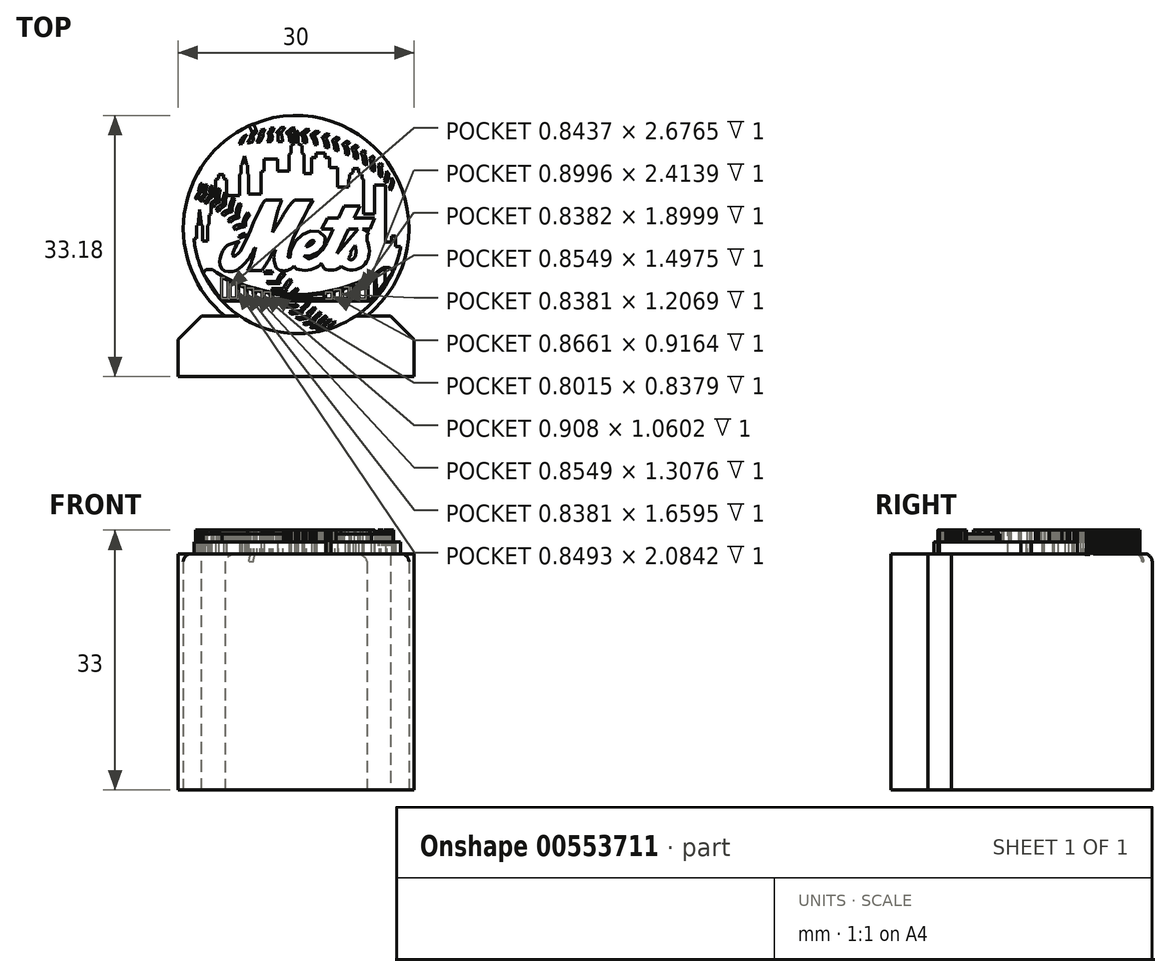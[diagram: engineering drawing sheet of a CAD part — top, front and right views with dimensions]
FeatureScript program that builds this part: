
annotation { "Feature Type Name" : "Feature", "Feature Type Description" : "" }
export const myFeature = defineFeature(function(context is Context, id is Id, definition is map)
    precondition{}
    {
        {
            var Q0;
            Q0=qCreatedBy(makeId("Top.planeOp"),FACE);
            var sketch = newSketch(context, id + "F0", { "sketchPlane" : qUnion([Q0])});
            skLineSegment(sketch, "E0", {"start": v(15.14, 30) * mm, "end": v(15.14, 0) * mm, "construction": true});
            skLineSegment(sketch, "E1", {"start": v(0, 15) * mm, "end": v(30.28, 15) * mm, "construction": true});
            skCircle(sketch, "E2", {"center": v(15.14, 15) * mm, "radius": 14.33 * mm});
            skLineSegment(sketch, "E3.bottom", {"start": v(30.14, -3.85) * mm, "end": v(0.14, -3.85) * mm});
            skLineSegment(sketch, "E3.top", {"start": v(30.14, 3.85) * mm, "end": v(0.14, 3.85) * mm});
            skLineSegment(sketch, "E3.left", {"start": v(30.14, -3.85) * mm, "end": v(30.14, 3.85) * mm});
            skLineSegment(sketch, "E3.right", {"start": v(0.14, -3.85) * mm, "end": v(0.14, 3.85) * mm});
            skPoint(sketch, "E3.middle", {"position": v(15.14, 0) * mm});
            skSolve(sketch);
        }
        {
            var Q0;
            Q0=makeQuery(id+"F0.imprint","IMPRINT",FACE,{"disambiguationData":[TD([[makeQuery(id+"F0.imprint","IMPRINT",EDGE,{"derivedFrom":sQuery(id+"F0.wireOp",EDGE,"E2")}),1.0]])]});
            var sketch = newSketch(context, id + "F1", { "sketchPlane" : qUnion([Q0])});
            skLineSegment(sketch, "E4", {"start": v(2.17, 13.7) * mm, "end": v(2.5, 13.7) * mm});
            skLineSegment(sketch, "E5", {"start": v(2.5, 13.7) * mm, "end": v(2.5, 15.34) * mm});
            skLineSegment(sketch, "E6", {"start": v(2.5, 15.34) * mm, "end": v(2.67, 15.34) * mm});
            skLineSegment(sketch, "E7", {"start": v(2.67, 15.34) * mm, "end": v(2.9, 17.39) * mm});
            skLineSegment(sketch, "E8", {"start": v(2.9, 17.39) * mm, "end": v(3.14, 15.34) * mm});
            skLineSegment(sketch, "E9", {"start": v(3.14, 15.34) * mm, "end": v(3.26, 15.34) * mm});
            skLineSegment(sketch, "E10", {"start": v(3.26, 15.34) * mm, "end": v(3.26, 13.38) * mm});
            skLineSegment(sketch, "E11", {"start": v(3.88, 13.38) * mm, "end": v(3.88, 15.34) * mm});
            skLineSegment(sketch, "E12", {"start": v(3.88, 15.34) * mm, "end": v(4.08, 15.57) * mm});
            skLineSegment(sketch, "E13", {"start": v(4.08, 15.57) * mm, "end": v(4.08, 16.67) * mm});
            skLineSegment(sketch, "E14", {"start": v(4.08, 16.67) * mm, "end": v(4.32, 16.83) * mm});
            skLineSegment(sketch, "E15", {"start": v(4.32, 16.83) * mm, "end": v(4.32, 18.27) * mm});
            skLineSegment(sketch, "E16", {"start": v(4.32, 18.27) * mm, "end": v(4.9, 18.66) * mm});
            skLineSegment(sketch, "E17", {"start": v(4.9, 18.66) * mm, "end": v(4.9, 21.2) * mm});
            skLineSegment(sketch, "E18", {"start": v(4.9, 21.2) * mm, "end": v(5.27, 21.3) * mm});
            skLineSegment(sketch, "E19", {"start": v(5.27, 21.3) * mm, "end": v(5.27, 21.8) * mm});
            skLineSegment(sketch, "E20", {"start": v(5.27, 21.8) * mm, "end": v(5.9, 21.8) * mm});
            skLineSegment(sketch, "E21", {"start": v(5.9, 21.8) * mm, "end": v(5.9, 21.3) * mm});
            skLineSegment(sketch, "E22", {"start": v(5.9, 21.3) * mm, "end": v(6.3, 21.2) * mm});
            skLineSegment(sketch, "E23", {"start": v(6.3, 21.2) * mm, "end": v(6.3, 19.15) * mm});
            skLineSegment(sketch, "E24", {"start": v(6.3, 19.15) * mm, "end": v(7.97, 19.15) * mm});
            skLineSegment(sketch, "E25", {"start": v(7.97, 19.15) * mm, "end": v(7.97, 21.8) * mm});
            skLineSegment(sketch, "E26", {"start": v(7.97, 21.8) * mm, "end": v(8.16, 21.93) * mm});
            skLineSegment(sketch, "E27", {"start": v(8.16, 21.93) * mm, "end": v(8.16, 23.04) * mm});
            skLineSegment(sketch, "E28", {"start": v(8.16, 23.04) * mm, "end": v(8.29, 23.13) * mm});
            skLineSegment(sketch, "E29", {"start": v(8.29, 23.13) * mm, "end": v(8.57, 24.2) * mm});
            skLineSegment(sketch, "E30", {"start": v(8.57, 24.2) * mm, "end": v(8.83, 23.13) * mm});
            skLineSegment(sketch, "E31", {"start": v(8.83, 23.13) * mm, "end": v(8.98, 23.04) * mm});
            skLineSegment(sketch, "E32", {"start": v(8.98, 23.04) * mm, "end": v(8.98, 21.93) * mm});
            skLineSegment(sketch, "E33", {"start": v(8.98, 21.93) * mm, "end": v(9.07, 21.8) * mm});
            skLineSegment(sketch, "E34", {"start": v(9.07, 21.8) * mm, "end": v(9.07, 19.34) * mm});
            skLineSegment(sketch, "E35", {"start": v(9.07, 19.34) * mm, "end": v(10.7, 19.34) * mm});
            skLineSegment(sketch, "E36", {"start": v(10.7, 19.34) * mm, "end": v(10.7, 22.18) * mm});
            skLineSegment(sketch, "E37", {"start": v(10.7, 22.18) * mm, "end": v(11.07, 22.27) * mm});
            skLineSegment(sketch, "E38", {"start": v(11.07, 22.27) * mm, "end": v(11.07, 23.8) * mm});
            skLineSegment(sketch, "E39", {"start": v(11.07, 23.8) * mm, "end": v(12.81, 23.8) * mm});
            skLineSegment(sketch, "E40", {"start": v(12.81, 23.8) * mm, "end": v(12.81, 22.27) * mm});
            skLineSegment(sketch, "E41", {"start": v(12.81, 22.27) * mm, "end": v(14.21, 22.27) * mm});
            skLineSegment(sketch, "E42", {"start": v(14.21, 22.27) * mm, "end": v(14.21, 24.34) * mm});
            skLineSegment(sketch, "E43", {"start": v(14.21, 24.34) * mm, "end": v(14.5, 24.54) * mm});
            skLineSegment(sketch, "E44", {"start": v(14.5, 24.54) * mm, "end": v(14.5, 25.5) * mm});
            skLineSegment(sketch, "E45", {"start": v(14.5, 25.5) * mm, "end": v(14.96, 25.8) * mm});
            skLineSegment(sketch, "E46", {"start": v(14.96, 25.8) * mm, "end": v(14.96, 27.25) * mm});
            skLineSegment(sketch, "E47", {"start": v(14.96, 27.25) * mm, "end": v(15.2, 27.4) * mm});
            skLineSegment(sketch, "E48", {"start": v(15.2, 27.4) * mm, "end": v(15.4, 27.25) * mm});
            skLineSegment(sketch, "E49", {"start": v(15.4, 27.25) * mm, "end": v(15.4, 25.8) * mm});
            skLineSegment(sketch, "E50", {"start": v(15.4, 25.8) * mm, "end": v(15.86, 25.5) * mm});
            skLineSegment(sketch, "E51", {"start": v(15.86, 25.5) * mm, "end": v(15.86, 24.54) * mm});
            skLineSegment(sketch, "E52", {"start": v(15.86, 24.54) * mm, "end": v(16.16, 24.34) * mm});
            skLineSegment(sketch, "E53", {"start": v(16.16, 24.34) * mm, "end": v(16.16, 21.93) * mm});
            skLineSegment(sketch, "E54", {"start": v(16.16, 21.93) * mm, "end": v(17.13, 21.93) * mm});
            skLineSegment(sketch, "E55", {"start": v(17.13, 21.93) * mm, "end": v(17.13, 23.96) * mm});
            skLineSegment(sketch, "E56", {"start": v(17.13, 23.96) * mm, "end": v(17.65, 23.96) * mm});
            skLineSegment(sketch, "E57", {"start": v(17.65, 23.96) * mm, "end": v(17.65, 24.54) * mm});
            skLineSegment(sketch, "E58", {"start": v(17.65, 24.54) * mm, "end": v(18.82, 24.54) * mm});
            skLineSegment(sketch, "E59", {"start": v(18.82, 24.54) * mm, "end": v(18.82, 23.96) * mm});
            skLineSegment(sketch, "E60", {"start": v(18.82, 23.96) * mm, "end": v(19.42, 23.96) * mm});
            skLineSegment(sketch, "E61", {"start": v(19.42, 23.96) * mm, "end": v(19.42, 22.73) * mm});
            skLineSegment(sketch, "E62", {"start": v(19.42, 22.73) * mm, "end": v(20.38, 22.73) * mm});
            skLineSegment(sketch, "E63", {"start": v(20.38, 22.73) * mm, "end": v(20.38, 20.24) * mm});
            skLineSegment(sketch, "E64", {"start": v(20.38, 20.24) * mm, "end": v(21.82, 20.24) * mm});
            skLineSegment(sketch, "E65", {"start": v(21.82, 20.24) * mm, "end": v(21.82, 21.2) * mm});
            skLineSegment(sketch, "E66", {"start": v(21.82, 21.2) * mm, "end": v(21.96, 21.3) * mm});
            skLineSegment(sketch, "E67", {"start": v(21.96, 21.3) * mm, "end": v(21.96, 21.8) * mm});
            skLineSegment(sketch, "E68", {"start": v(21.96, 21.8) * mm, "end": v(22.38, 22.08) * mm});
            skLineSegment(sketch, "E69", {"start": v(22.38, 22.08) * mm, "end": v(22.38, 22.58) * mm});
            skLineSegment(sketch, "E70", {"start": v(22.38, 22.58) * mm, "end": v(23.09, 22.58) * mm});
            skLineSegment(sketch, "E71", {"start": v(23.09, 22.58) * mm, "end": v(23.09, 22.08) * mm});
            skLineSegment(sketch, "E72", {"start": v(23.09, 22.08) * mm, "end": v(23.5, 21.8) * mm});
            skLineSegment(sketch, "E73", {"start": v(23.5, 21.8) * mm, "end": v(23.5, 21.3) * mm});
            skLineSegment(sketch, "E74", {"start": v(23.5, 21.3) * mm, "end": v(23.69, 21.2) * mm});
            skLineSegment(sketch, "E75", {"start": v(23.69, 21.2) * mm, "end": v(23.69, 16.83) * mm});
            skLineSegment(sketch, "E76", {"start": v(23.69, 16.83) * mm, "end": v(25.08, 16.83) * mm});
            skLineSegment(sketch, "E77", {"start": v(25.08, 16.83) * mm, "end": v(25.08, 20.5) * mm});
            skLineSegment(sketch, "E78", {"start": v(25.08, 20.5) * mm, "end": v(26.53, 20.5) * mm});
            skLineSegment(sketch, "E79", {"start": v(26.53, 20.5) * mm, "end": v(26.53, 13.29) * mm});
            skLineSegment(sketch, "E80", {"start": v(26.53, 13.29) * mm, "end": v(27.26, 13.29) * mm});
            skLineSegment(sketch, "E81", {"start": v(27.26, 13.29) * mm, "end": v(27.26, 14) * mm});
            skLineSegment(sketch, "E82", {"start": v(27.26, 14) * mm, "end": v(27.74, 14) * mm});
            skLineSegment(sketch, "E83", {"start": v(27.74, 14) * mm, "end": v(27.74, 12.66) * mm});
            skLineSegment(sketch, "E84", {"start": v(27.74, 12.66) * mm, "end": v(28.41, 12.66) * mm});
            skArc(sketch, "E85", {"start": v(2.17, 13.7) * mm, "mid": v(14.83, 1.63) * mm, "end": v(28.41, 12.66) * mm});
            skLineSegment(sketch, "E86", {"start": v(3.26, 13.38) * mm, "end": v(3.88, 13.38) * mm});
            skSolve(sketch);
        }
        {
            var Q0;
            Q0=makeQuery(id+"F0.imprint","IMPRINT",FACE,{"disambiguationData":[TD([[makeQuery(id+"F0.imprint","IMPRINT",EDGE,{"derivedFrom":sQuery(id+"F0.wireOp",EDGE,"E2")}),1.0]])]});
            var sketch = newSketch(context, id + "F2", { "sketchPlane" : qUnion([Q0])});
            skLineSegment(sketch, "E87", {"start": v(11.25, 18.59) * mm, "end": v(13.33, 18.59) * mm});
            skFitSpline(sketch, "E88", {"points": [v(13.33, 18.59) * mm, v(13.16, 18.19) * mm, v(12.79, 17.17) * mm, v(12.52, 16.09) * mm], "startDerivative": vector(-0.65, -1.46) * mm, "endDerivative": vector(-0.62, -2.77) * mm});
            skLineSegment(sketch, "E89", {"start": v(12.52, 16.09) * mm, "end": v(12.14, 14.47) * mm});
            skFitSpline(sketch, "E90", {"points": [v(12.14, 14.47) * mm, v(12.55, 15.14) * mm, v(13.14, 16.08) * mm, v(13.74, 17.05) * mm, v(14.35, 17.93) * mm, v(14.92, 18.59) * mm], "startDerivative": vector(2.21, 3.58) * mm, "endDerivative": vector(3.06, 3.36) * mm});
            skLineSegment(sketch, "E91", {"start": v(14.92, 18.59) * mm, "end": v(17.26, 18.59) * mm});
            skFitSpline(sketch, "E92", {"points": [v(17.26, 18.59) * mm, v(16.82, 17.86) * mm, v(16.11, 16.48) * mm, v(15.3, 14.87) * mm, v(14.62, 13.31) * mm, v(14.19, 12.01) * mm, v(14.15, 11.26) * mm, v(14.28, 11.16) * mm, v(14.38, 11.2) * mm, v(14.4, 11.47) * mm, v(14.53, 12.4) * mm, v(15.1, 13.42) * mm, v(15.87, 14.15) * mm, v(16.83, 14.6) * mm, v(17.7, 14.67) * mm, v(18.49, 14.32) * mm, v(18.9, 13.57) * mm, v(18.6, 12.67) * mm, v(17.94, 12) * mm, v(17.26, 11.64) * mm, v(16.34, 11.43) * mm, v(16.16, 11.44) * mm, v(16.35, 11.18) * mm, v(16.97, 11.16) * mm, v(17.86, 11.6) * mm, v(18.4, 12.16) * mm, v(18.9, 12.9) * mm, v(19.3, 13.69) * mm, v(19.72, 14.57) * mm, v(19.85, 14.9) * mm], "startDerivative": vector(-11.95, -18.74) * mm, "endDerivative": vector(4.49, 12.3) * mm});
            skLineSegment(sketch, "E93", {"start": v(19.85, 14.9) * mm, "end": v(18.38, 14.9) * mm});
            skLineSegment(sketch, "E94", {"start": v(18.38, 14.9) * mm, "end": v(19.11, 16.29) * mm});
            skLineSegment(sketch, "E95", {"start": v(19.11, 16.29) * mm, "end": v(20.53, 16.29) * mm});
            skLineSegment(sketch, "E96", {"start": v(20.53, 16.29) * mm, "end": v(21.26, 17.85) * mm});
            skLineSegment(sketch, "E97", {"start": v(21.26, 17.85) * mm, "end": v(23.24, 17.85) * mm});
            skLineSegment(sketch, "E98", {"start": v(23.24, 17.85) * mm, "end": v(22.51, 16.29) * mm});
            skLineSegment(sketch, "E99", {"start": v(22.51, 16.29) * mm, "end": v(25.07, 16.29) * mm});
            skLineSegment(sketch, "E100", {"start": v(25.07, 16.29) * mm, "end": v(24.52, 14.9) * mm});
            skLineSegment(sketch, "E101", {"start": v(24.52, 14.9) * mm, "end": v(23.6, 14.9) * mm});
            skLineSegment(sketch, "E102", {"start": v(23.6, 14.9) * mm, "end": v(24.38, 14.48) * mm});
            skFitSpline(sketch, "E103", {"points": [v(24.38, 14.48) * mm, v(24.14, 14.06) * mm, v(24.2, 13.36) * mm, v(24.42, 12.5) * mm, v(24.38, 11.45) * mm, v(24.01, 10.62) * mm, v(23.3, 9.99) * mm, v(22.4, 9.73) * mm, v(21.45, 9.83) * mm, v(20.86, 10.21) * mm], "startDerivative": vector(-3.57, -4.54) * mm, "endDerivative": vector(-5.2, 4.27) * mm});
            skFitSpline(sketch, "E104", {"points": [v(20.86, 10.21) * mm, v(20.5, 9.88) * mm, v(19.8, 9.72) * mm, v(18.98, 9.78) * mm, v(18.54, 10.11) * mm, v(18.3, 10.5) * mm, v(18.02, 10.21) * mm, v(17.31, 9.87) * mm, v(16.27, 9.66) * mm, v(15.21, 9.86) * mm, v(14.85, 10.21) * mm], "startDerivative": vector(-3.77, -4.27) * mm, "endDerivative": vector(-3.25, 4.4) * mm});
            skFitSpline(sketch, "E105", {"points": [v(14.85, 10.21) * mm, v(14.47, 9.85) * mm, v(13.77, 9.6) * mm, v(12.9, 9.74) * mm, v(12.5, 10.25) * mm, v(12.31, 11) * mm, v(12.34, 11.75) * mm, v(12.5, 12.33) * mm], "startDerivative": vector(-2.74, -3.06) * mm, "endDerivative": vector(1.37, 4.22) * mm});
            skFitSpline(sketch, "E106", {"points": [v(12.5, 12.33) * mm, v(12.2, 11.97) * mm, v(11.81, 11.26) * mm, v(11.34, 10.46) * mm, v(10.79, 9.66) * mm], "startDerivative": vector(-1.57, -1.66) * mm, "endDerivative": vector(-2, -2.88) * mm});
            skLineSegment(sketch, "E107", {"start": v(10.79, 9.66) * mm, "end": v(8.95, 9.66) * mm});
            skFitSpline(sketch, "E108", {"points": [v(8.95, 9.66) * mm, v(9.23, 10.1) * mm, v(9.6, 11.13) * mm, v(9.87, 12.07) * mm, v(9.98, 12.53) * mm], "startDerivative": vector(1.33, 1.86) * mm, "endDerivative": vector(0.48, 2.12) * mm});
            skFitSpline(sketch, "E109", {"points": [v(9.98, 12.53) * mm, v(9.87, 12.49) * mm, v(9.7, 12.08) * mm, v(9.37, 11.52) * mm, v(8.95, 10.9) * mm, v(8.22, 10.12) * mm, v(7.56, 9.66) * mm, v(6.69, 9.48) * mm, v(5.8, 9.75) * mm, v(5.44, 10.5) * mm, v(5.5, 11.17) * mm, v(5.75, 11.94) * mm, v(6.26, 12.74) * mm, v(6.49, 12.9) * mm, v(7.95, 13.4) * mm], "startDerivative": vector(-4.02, -0.49) * mm, "endDerivative": vector(17.33, 5.86) * mm});
            skFitSpline(sketch, "E110", {"points": [v(7.95, 13.4) * mm, v(7.69, 13.04) * mm, v(7.38, 12.53) * mm, v(7.14, 11.96) * mm, v(7.1, 11.57) * mm, v(7.24, 11.43) * mm, v(7.63, 11.65) * mm, v(8.12, 12.28) * mm, v(8.95, 13.9) * mm, v(9.58, 15.35) * mm, v(10.18, 16.7) * mm, v(10.99, 18.3) * mm, v(11.25, 18.59) * mm], "startDerivative": vector(-4.1, -5.58) * mm, "endDerivative": vector(4.03, 3.58) * mm});
            skSolve(sketch);
        }
        {
            var Q0;
            Q0=qSketchRegion(id+"F0",true);
            extrude(context, id + "F3", {"entities" : qUnion([Q0]), "depth" : 30 * mm, "offsetDistance" : 25.4 * mm});
        }
        {
            var Q0;
            Q0=qSketchRegion(id+"F1",true);
            extrude(context, id + "F4", {"entities" : qUnion([Q0]), "operationType" : NewBodyOperationType.ADD, "depth" : 31.5 * mm, "offsetDistance" : 25.4 * mm});
        }
        {
            var Q0;
            Q0=makeQuery(id+"F3.opExtrude","CAP_FACE",FACE,{"disambiguationData":[OSD([sQuery(id+"F0.wireOp",EDGE,"E2")])],"isStart":false});
            var sketch = newSketch(context, id + "F5", { "sketchPlane" : qUnion([Q0])});
            skFitSpline(sketch, "E111", {"points": [v(16.4, 12.67) * mm, v(16.47, 12.86) * mm, v(16.72, 13.14) * mm, v(17.02, 13.37) * mm, v(17.35, 13.43) * mm, v(17.42, 13.34) * mm, v(17.31, 13.15) * mm, v(16.98, 12.9) * mm, v(16.64, 12.72) * mm, v(16.4, 12.67) * mm]});
            skLineSegment(sketch, "E112", {"start": v(20.32, 11.78) * mm, "end": v(21.8, 14.92) * mm});
            skLineSegment(sketch, "E113", {"start": v(21.8, 14.92) * mm, "end": v(22.98, 14.92) * mm});
            skLineSegment(sketch, "E114", {"start": v(22.98, 14.92) * mm, "end": v(20.32, 11.78) * mm});
            skLineSegment(sketch, "E115", {"start": v(22, 11.95) * mm, "end": v(22.63, 12.83) * mm});
            skFitSpline(sketch, "E116", {"points": [v(22.63, 12.83) * mm, v(22.68, 12.73) * mm, v(22.71, 12.47) * mm, v(22.73, 12) * mm, v(22.68, 11.54) * mm, v(22.52, 11.25) * mm, v(22.2, 11.01) * mm, v(21.9, 11.05) * mm, v(21.83, 11.25) * mm, v(21.97, 11.51) * mm, v(22.19, 11.74) * mm], "startDerivative": vector(0.88, -1.53) * mm, "endDerivative": vector(2.11, 2.19) * mm});
            skLineSegment(sketch, "E117", {"start": v(22.19, 11.74) * mm, "end": v(22, 11.95) * mm});
            skSolve(sketch);
        }
        {
            var Q0;
            Q0=qSketchRegion(id+"F2",true);
            extrude(context, id + "F6", {"entities" : qUnion([Q0]), "operationType" : NewBodyOperationType.ADD, "depth" : 33 * mm, "offsetDistance" : 25.4 * mm});
        }
        {
            var Q0;
            Q0=qSketchRegion(id+"F5",true);
            extrude(context, id + "F7", {"entities" : qUnion([Q0]), "operationType" : NewBodyOperationType.REMOVE, "depth" : 25.4 * mm, "offsetDistance" : 25.4 * mm});
        }
        {
            var Q0;
            Q0=makeQuery(id+"F3.opExtrude","CAP_FACE",FACE,{"disambiguationData":[OSD([sQuery(id+"F0.wireOp",EDGE,"E2")])],"isStart":false});
            var sketch = newSketch(context, id + "F8", { "sketchPlane" : qUnion([Q0])});
            skLineSegment(sketch, "E118", {"start": v(3.02, 20.66) * mm, "end": v(3.17, 20.66) * mm});
            skFitSpline(sketch, "E119", {"points": [v(3.17, 20.66) * mm, v(3.1, 20.34) * mm, v(2.99, 19.94) * mm, v(3.08, 19.57) * mm], "startDerivative": vector(-0.2, -0.98) * mm, "endDerivative": vector(0.43, -1.08) * mm});
            skFitSpline(sketch, "E120", {"points": [v(3.08, 19.57) * mm, v(2.89, 19.37) * mm, v(2.67, 18.96) * mm, v(2.55, 18.65) * mm], "startDerivative": vector(-0.64, -0.58) * mm, "endDerivative": vector(-0.32, -0.88) * mm});
            skLineSegment(sketch, "E121", {"start": v(2.55, 18.65) * mm, "end": v(2.36, 18.77) * mm});
            skFitSpline(sketch, "E122", {"points": [v(2.36, 18.77) * mm, v(2.48, 19.12) * mm, v(2.66, 19.41) * mm, v(2.84, 19.61) * mm], "startDerivative": vector(0.3, 1) * mm, "endDerivative": vector(0.6, 0.6) * mm});
            skFitSpline(sketch, "E123", {"points": [v(2.84, 19.61) * mm, v(2.78, 19.78) * mm, v(2.84, 20.15) * mm, v(2.9, 20.34) * mm, v(3.02, 20.66) * mm], "startDerivative": vector(-0.4, 0.7) * mm, "endDerivative": vector(0.4, 1.24) * mm});
            skLineSegment(sketch, "E124", {"start": v(3.55, 20.59) * mm, "end": v(3.84, 20.51) * mm});
            skFitSpline(sketch, "E125", {"points": [v(3.84, 20.51) * mm, v(3.71, 19.96) * mm, v(3.66, 19.55) * mm, v(3.74, 19.3) * mm], "startDerivative": vector(-0.33, -1.42) * mm, "endDerivative": vector(0.4, -0.87) * mm});
            skFitSpline(sketch, "E126", {"points": [v(3.74, 19.3) * mm, v(3.54, 19.08) * mm, v(3.3, 18.76) * mm, v(3.13, 18.4) * mm], "startDerivative": vector(-0.6, -0.74) * mm, "endDerivative": vector(-0.38, -1.09) * mm});
            skLineSegment(sketch, "E127", {"start": v(3.13, 18.4) * mm, "end": v(2.93, 18.52) * mm});
            skFitSpline(sketch, "E128", {"points": [v(2.93, 18.52) * mm, v(3.07, 18.88) * mm, v(3.47, 19.32) * mm], "startDerivative": vector(0.22, 0.82) * mm, "endDerivative": vector(0.84, 0.79) * mm});
            skFitSpline(sketch, "E129", {"points": [v(3.47, 19.32) * mm, v(3.38, 19.62) * mm, v(3.4, 20.05) * mm, v(3.55, 20.59) * mm], "startDerivative": vector(-0.36, 1) * mm, "endDerivative": vector(0.44, 1.42) * mm});
            skLineSegment(sketch, "E130", {"start": v(4.32, 20.4) * mm, "end": v(4.6, 20.26) * mm});
            skFitSpline(sketch, "E131", {"points": [v(4.6, 20.26) * mm, v(4.5, 19.85) * mm, v(4.45, 19.32) * mm, v(4.52, 18.96) * mm], "startDerivative": vector(-0.32, -1.18) * mm, "endDerivative": vector(0.3, -1.1) * mm});
            skFitSpline(sketch, "E132", {"points": [v(4.52, 18.96) * mm, v(4.32, 18.83) * mm, v(4.05, 18.58) * mm, v(3.8, 18.13) * mm], "startDerivative": vector(-0.7, -0.44) * mm, "endDerivative": vector(-0.54, -1.23) * mm});
            skLineSegment(sketch, "E133", {"start": v(3.8, 18.13) * mm, "end": v(3.5, 18.27) * mm});
            skFitSpline(sketch, "E134", {"points": [v(3.5, 18.27) * mm, v(3.64, 18.53) * mm, v(3.98, 18.91) * mm, v(4.17, 19.05) * mm], "startDerivative": vector(0.38, 0.76) * mm, "endDerivative": vector(0.65, 0.37) * mm});
            skFitSpline(sketch, "E135", {"points": [v(4.17, 19.05) * mm, v(4.12, 19.36) * mm, v(4.17, 19.92) * mm, v(4.32, 20.4) * mm], "startDerivative": vector(-0.24, 1.02) * mm, "endDerivative": vector(0.47, 1.3) * mm});
            skLineSegment(sketch, "E136", {"start": v(5.2, 20.05) * mm, "end": v(5.5, 19.9) * mm});
            skFitSpline(sketch, "E137", {"points": [v(5.5, 19.9) * mm, v(5.42, 19.54) * mm, v(5.38, 18.87) * mm, v(5.53, 18.4) * mm], "startDerivative": vector(-0.3, -1.13) * mm, "endDerivative": vector(0.6, -1.3) * mm});
            skFitSpline(sketch, "E138", {"points": [v(5.53, 18.4) * mm, v(5.29, 18.3) * mm, v(4.97, 18.05) * mm, v(4.64, 17.64) * mm], "startDerivative": vector(-0.87, -0.3) * mm, "endDerivative": vector(-0.82, -1.1) * mm});
            skLineSegment(sketch, "E139", {"start": v(4.64, 17.64) * mm, "end": v(4.37, 17.85) * mm});
            skFitSpline(sketch, "E140", {"points": [v(4.37, 17.85) * mm, v(4.43, 18.04) * mm, v(4.8, 18.37) * mm, v(5.16, 18.57) * mm], "startDerivative": vector(0.13, 0.73) * mm, "endDerivative": vector(0.96, 0.49) * mm});
            skFitSpline(sketch, "E141", {"points": [v(5.16, 18.57) * mm, v(5.1, 18.97) * mm, v(5.06, 19.58) * mm, v(5.2, 20.05) * mm], "startDerivative": vector(-0.23, 1.25) * mm, "endDerivative": vector(0.52, 1.35) * mm});
            skLineSegment(sketch, "E142", {"start": v(6.07, 19.58) * mm, "end": v(6.4, 19.42) * mm});
            skFitSpline(sketch, "E143", {"points": [v(6.4, 19.42) * mm, v(6.32, 19.2) * mm, v(6.23, 18.88) * mm, v(6.16, 18.29) * mm, v(6.22, 17.95) * mm], "startDerivative": vector(-0.36, -1.04) * mm, "endDerivative": vector(0.37, -1.27) * mm});
            skFitSpline(sketch, "E144", {"points": [v(6.22, 17.95) * mm, v(5.96, 17.82) * mm, v(5.6, 17.53) * mm, v(5.52, 17.44) * mm, v(5.34, 17.15) * mm], "startDerivative": vector(-0.95, -0.37) * mm, "endDerivative": vector(-0.78, -1.25) * mm});
            skLineSegment(sketch, "E145", {"start": v(5.34, 17.15) * mm, "end": v(5.05, 17.34) * mm});
            skFitSpline(sketch, "E146", {"points": [v(5.05, 17.34) * mm, v(5.11, 17.57) * mm, v(5.56, 17.94) * mm, v(5.9, 18.13) * mm], "startDerivative": vector(0.05, 0.86) * mm, "endDerivative": vector(0.96, 0.5) * mm});
            skFitSpline(sketch, "E147", {"points": [v(5.9, 18.13) * mm, v(5.84, 18.46) * mm, v(5.9, 18.98) * mm, v(6.07, 19.58) * mm], "startDerivative": vector(-0.32, 1.11) * mm, "endDerivative": vector(0.47, 1.59) * mm});
            skLineSegment(sketch, "E148", {"start": v(7.06, 18.88) * mm, "end": v(7.37, 18.65) * mm});
            skPoint(sketch, "E149.1.internal.snap0", {"position": v(7.22, 18.76) * mm});
            skFitSpline(sketch, "E149", {"points": [v(7.37, 18.65) * mm, v(7.22, 18.36) * mm, v(7.05, 17.8) * mm, v(6.98, 17.34) * mm, v(7.1, 17.18) * mm], "startDerivative": vector(-0.7, -1.12) * mm, "endDerivative": vector(0.8, -0.76) * mm});
            skFitSpline(sketch, "E150", {"points": [v(7.1, 17.18) * mm, v(6.85, 17.1) * mm, v(6.42, 16.94) * mm, v(6, 16.61) * mm], "startDerivative": vector(-0.86, -0.28) * mm, "endDerivative": vector(-1.07, -0.96) * mm});
            skLineSegment(sketch, "E151", {"start": v(6, 16.61) * mm, "end": v(5.7, 16.82) * mm});
            skFitSpline(sketch, "E152", {"points": [v(5.7, 16.82) * mm, v(5.9, 17.06) * mm, v(6.38, 17.29) * mm, v(6.83, 17.45) * mm], "startDerivative": vector(0.55, 0.92) * mm, "endDerivative": vector(1.23, 0.43) * mm});
            skFitSpline(sketch, "E153", {"points": [v(6.83, 17.45) * mm, v(6.72, 17.6) * mm, v(6.74, 18.04) * mm, v(6.88, 18.47) * mm, v(7.06, 18.88) * mm], "startDerivative": vector(-0.74, 0.74) * mm, "endDerivative": vector(0.7, 1.48) * mm});
            skLineSegment(sketch, "E154", {"start": v(7.9, 18.24) * mm, "end": v(8.2, 17.95) * mm});
            skFitSpline(sketch, "E155", {"points": [v(8.2, 17.95) * mm, v(8.07, 17.72) * mm, v(7.88, 17.04) * mm, v(7.82, 16.59) * mm, v(7.92, 16.35) * mm], "startDerivative": vector(-0.64, -0.94) * mm, "endDerivative": vector(0.6, -1.12) * mm});
            skFitSpline(sketch, "E156", {"points": [v(7.92, 16.35) * mm, v(7.63, 16.28) * mm, v(7.2, 16.07) * mm, v(6.87, 15.86) * mm, v(6.75, 15.72) * mm], "startDerivative": vector(-1.15, -0.2) * mm, "endDerivative": vector(-0.55, -0.71) * mm});
            skLineSegment(sketch, "E157", {"start": v(6.75, 15.72) * mm, "end": v(6.51, 16.01) * mm});
            skFitSpline(sketch, "E158", {"points": [v(6.51, 16.01) * mm, v(6.66, 16.2) * mm, v(7.14, 16.48) * mm, v(7.61, 16.66) * mm], "startDerivative": vector(0.45, 0.77) * mm, "endDerivative": vector(1.25, 0.43) * mm});
            skFitSpline(sketch, "E159", {"points": [v(7.61, 16.66) * mm, v(7.55, 16.8) * mm, v(7.57, 17.34) * mm, v(7.72, 17.86) * mm, v(7.9, 18.24) * mm], "startDerivative": vector(-0.47, 0.78) * mm, "endDerivative": vector(0.7, 1.44) * mm});
            skLineSegment(sketch, "E160", {"start": v(8.98, 17) * mm, "end": v(9.24, 16.67) * mm});
            skFitSpline(sketch, "E161", {"points": [v(9.24, 16.67) * mm, v(9.04, 16.4) * mm, v(8.74, 15.84) * mm, v(8.7, 15.36) * mm, v(8.72, 15.24) * mm], "startDerivative": vector(-0.8, -0.96) * mm, "endDerivative": vector(0.17, -0.68) * mm});
            skFitSpline(sketch, "E162", {"points": [v(8.72, 15.24) * mm, v(8.46, 15.19) * mm, v(7.87, 15.04) * mm, v(7.44, 14.8) * mm], "startDerivative": vector(-0.89, -0.18) * mm, "endDerivative": vector(-1.11, -0.76) * mm});
            skLineSegment(sketch, "E163", {"start": v(7.44, 14.8) * mm, "end": v(7.18, 15.12) * mm});
            skFitSpline(sketch, "E164", {"points": [v(7.18, 15.12) * mm, v(7.57, 15.4) * mm, v(8.17, 15.48) * mm, v(8.45, 15.55) * mm], "startDerivative": vector(0.97, 0.97) * mm, "endDerivative": vector(0.89, 0.32) * mm});
            skFitSpline(sketch, "E165", {"points": [v(8.45, 15.55) * mm, v(8.38, 15.75) * mm, v(8.49, 16.1) * mm, v(8.62, 16.45) * mm, v(8.98, 17) * mm], "startDerivative": vector(-0.56, 0.99) * mm, "endDerivative": vector(1.3, 1.73) * mm});
            skLineSegment(sketch, "E166", {"start": v(7.86, 14.02) * mm, "end": v(7.98, 13.74) * mm});
            skFitSpline(sketch, "E167", {"points": [v(7.98, 13.74) * mm, v(8.22, 13.86) * mm, v(8.68, 14.01) * mm], "startDerivative": vector(0.52, 0.3) * mm, "endDerivative": vector(0.88, 0.26) * mm});
            skLineSegment(sketch, "E168", {"start": v(8.68, 14.01) * mm, "end": v(8.68, 14.34) * mm});
            skFitSpline(sketch, "E169", {"points": [v(8.68, 14.34) * mm, v(8.35, 14.27) * mm, v(7.86, 14.02) * mm], "startDerivative": vector(-0.73, -0.1) * mm, "endDerivative": vector(-0.9, -0.54) * mm});
            skLineSegment(sketch, "E170", {"start": v(11.27, 9.54) * mm, "end": v(11.05, 9.26) * mm});
            skLineSegment(sketch, "E171", {"start": v(11.05, 9.26) * mm, "end": v(12.14, 9.26) * mm});
            skLineSegment(sketch, "E172", {"start": v(11.27, 9.54) * mm, "end": v(12.07, 9.54) * mm});
            skLineSegment(sketch, "E173", {"start": v(12.07, 9.54) * mm, "end": v(12.14, 9.26) * mm});
            skLineSegment(sketch, "E174", {"start": v(11.38, 8.25) * mm, "end": v(11.62, 7.93) * mm});
            skLineSegment(sketch, "E175", {"start": v(11.62, 7.93) * mm, "end": v(13.11, 7.96) * mm});
            skFitSpline(sketch, "E176", {"points": [v(13.11, 7.96) * mm, v(13.07, 8.08) * mm, v(13.06, 8.37) * mm, v(13.4, 8.79) * mm, v(13.79, 9.25) * mm], "startDerivative": vector(-0.34, 0.71) * mm, "endDerivative": vector(1.18, 1.44) * mm});
            skLineSegment(sketch, "E177", {"start": v(13.79, 9.25) * mm, "end": v(13.31, 9.28) * mm});
            skFitSpline(sketch, "E178", {"points": [v(13.31, 9.28) * mm, v(13.07, 9.05) * mm, v(12.78, 8.52) * mm, v(12.75, 8.33) * mm], "startDerivative": vector(-0.73, -0.58) * mm, "endDerivative": vector(0, -0.67) * mm});
            skLineSegment(sketch, "E179", {"start": v(11.38, 8.25) * mm, "end": v(12.75, 8.33) * mm});
            skLineSegment(sketch, "E180", {"start": v(14.36, 8.56) * mm, "end": v(14.63, 8.22) * mm});
            skFitSpline(sketch, "E181", {"points": [v(14.63, 8.22) * mm, v(14.35, 7.95) * mm, v(13.93, 7.36) * mm, v(13.83, 7.23) * mm, v(14, 6.98) * mm], "startDerivative": vector(-1.06, -0.8) * mm, "endDerivative": vector(1.15, -1.24) * mm});
            skFitSpline(sketch, "E182", {"points": [v(14, 6.98) * mm, v(13.85, 6.93) * mm, v(13.4, 6.98) * mm, v(12.8, 6.98) * mm, v(12.21, 6.98) * mm], "startDerivative": vector(-0.87, -0.44) * mm, "endDerivative": vector(-1.99, 0.03) * mm});
            skLineSegment(sketch, "E183", {"start": v(12.21, 6.98) * mm, "end": v(12, 7.32) * mm});
            skLineSegment(sketch, "E184", {"start": v(12, 7.32) * mm, "end": v(13.55, 7.32) * mm});
            skFitSpline(sketch, "E185", {"points": [v(13.55, 7.32) * mm, v(13.6, 7.54) * mm, v(13.78, 7.88) * mm, v(14.09, 8.29) * mm, v(14.36, 8.56) * mm], "startDerivative": vector(0.17, 1.08) * mm, "endDerivative": vector(1.05, 1) * mm});
            skLineSegment(sketch, "E186", {"start": v(15.18, 7.45) * mm, "end": v(15.4, 7.24) * mm});
            skFitSpline(sketch, "E187", {"points": [v(15.4, 7.24) * mm, v(15.23, 7) * mm, v(14.8, 6.6) * mm, v(14.5, 6.76) * mm], "startDerivative": vector(-0.49, -0.72) * mm, "endDerivative": vector(-0.92, 0.87) * mm});
            skLineSegment(sketch, "E188", {"start": v(14.5, 6.76) * mm, "end": v(15.18, 7.45) * mm});
            skLineSegment(sketch, "E189", {"start": v(13.55, 5.26) * mm, "end": v(13.77, 5) * mm});
            skLineSegment(sketch, "E190", {"start": v(13.77, 5) * mm, "end": v(14.73, 5) * mm});
            skFitSpline(sketch, "E191", {"points": [v(14.73, 5) * mm, v(15.33, 5.1) * mm, v(15.4, 5.2) * mm], "startDerivative": vector(1.08, 0.09) * mm, "endDerivative": vector(0.11, 0.34) * mm});
            skLineSegment(sketch, "E192", {"start": v(15.4, 5.2) * mm, "end": v(15.21, 5.35) * mm});
            skFitSpline(sketch, "E193", {"points": [v(13.55, 5.26) * mm, v(14.09, 5.26) * mm, v(14.81, 5.26) * mm, v(15.21, 5.35) * mm], "startDerivative": vector(1.52, 0.02) * mm, "endDerivative": vector(1.25, 0.39) * mm});
            skLineSegment(sketch, "E194", {"start": v(15.68, 4.81) * mm, "end": v(15.89, 4.6) * mm});
            skFitSpline(sketch, "E195", {"points": [v(15.89, 4.6) * mm, v(16.18, 4.75) * mm, v(16.73, 5.31) * mm, v(16.88, 5.54) * mm], "startDerivative": vector(0.9, 0.38) * mm, "endDerivative": vector(0.4, 0.75) * mm});
            skLineSegment(sketch, "E196", {"start": v(16.88, 5.54) * mm, "end": v(16.63, 5.76) * mm});
            skFitSpline(sketch, "E197", {"points": [v(15.68, 4.81) * mm, v(16.03, 5.04) * mm, v(16.38, 5.4) * mm, v(16.63, 5.76) * mm], "startDerivative": vector(1.11, 0.64) * mm, "endDerivative": vector(0.71, 1.1) * mm});
            skLineSegment(sketch, "E198", {"start": v(14.25, 4.43) * mm, "end": v(14.51, 4.14) * mm});
            skLineSegment(sketch, "E199", {"start": v(15.06, 3.67) * mm, "end": v(15.44, 3.39) * mm});
            skFitSpline(sketch, "E200", {"points": [v(15.44, 3.39) * mm, v(15.92, 3.45) * mm, v(16.94, 3.69) * mm], "startDerivative": vector(1.08, 0.11) * mm, "endDerivative": vector(1.88, 0.46) * mm});
            skFitSpline(sketch, "E201", {"points": [v(15.06, 3.67) * mm, v(15.73, 3.67) * mm, v(16.66, 3.92) * mm], "startDerivative": vector(1.43, -0.1) * mm, "endDerivative": vector(1.77, 0.59) * mm});
            skLineSegment(sketch, "E202", {"start": v(17.4, 5.01) * mm, "end": v(17.62, 4.81) * mm});
            skPoint(sketch, "E203.2.internal.snap0", {"position": v(16.8, 3.8) * mm});
            skLineSegment(sketch, "E204", {"start": v(16.66, 3.92) * mm, "end": v(16.47, 4.08) * mm});
            skLineSegment(sketch, "E205", {"start": v(16.47, 4.08) * mm, "end": v(17.4, 5.01) * mm});
            skLineSegment(sketch, "E206", {"start": v(16.04, 2.93) * mm, "end": v(16.41, 2.74) * mm});
            skLineSegment(sketch, "E207", {"start": v(18.09, 4.39) * mm, "end": v(18.36, 4.17) * mm});
            skFitSpline(sketch, "E208", {"points": [v(17.22, 3.52) * mm, v(17.5, 3.76) * mm, v(17.87, 4.1) * mm, v(18.09, 4.39) * mm], "startDerivative": vector(0.85, 0.7) * mm, "endDerivative": vector(0.6, 0.93) * mm});
            skFitSpline(sketch, "E209", {"points": [v(16.89, 2.53) * mm, v(17.22, 2.34) * mm], "startDerivative": vector(0.33, -0.18) * mm, "endDerivative": vector(0.33, -0.18) * mm});
            skFitSpline(sketch, "E210", {"points": [v(17.22, 2.34) * mm, v(17.7, 2.48) * mm, v(18.23, 2.86) * mm, v(18.21, 3.06) * mm], "startDerivative": vector(1.21, 0.26) * mm, "endDerivative": vector(-0.35, 0.84) * mm});
            skFitSpline(sketch, "E211", {"points": [v(18.21, 3.06) * mm, v(18.48, 3.17) * mm, v(19.03, 3.7) * mm, v(18.82, 3.87) * mm], "startDerivative": vector(0.76, 0.22) * mm, "endDerivative": vector(-1.2, 0.49) * mm});
            skFitSpline(sketch, "E212", {"points": [v(18.82, 3.87) * mm, v(18.59, 3.67) * mm, v(18.09, 3.28) * mm, v(17.95, 3.2) * mm], "startDerivative": vector(-0.6, -0.54) * mm, "endDerivative": vector(-0.48, -0.2) * mm});
            skFitSpline(sketch, "E213", {"points": [v(16.89, 2.53) * mm, v(17.22, 2.61) * mm, v(17.95, 2.93) * mm, v(17.95, 3.2) * mm], "startDerivative": vector(0.9, 0.24) * mm, "endDerivative": vector(-0.37, 1.1) * mm});
            skLineSegment(sketch, "E214", {"start": v(19.44, 3.48) * mm, "end": v(19.62, 3.34) * mm});
            skFitSpline(sketch, "E215", {"points": [v(19.44, 3.48) * mm, v(19.03, 3.1) * mm, v(18.65, 2.86) * mm], "startDerivative": vector(-0.77, -0.79) * mm, "endDerivative": vector(-0.82, -0.44) * mm});
            skFitSpline(sketch, "E216", {"points": [v(18.65, 2.86) * mm, v(18.65, 2.76) * mm, v(18.46, 2.55) * mm, v(18, 2.3) * mm, v(17.65, 2.2) * mm], "startDerivative": vector(0.13, -0.62) * mm, "endDerivative": vector(-1.19, -0.3) * mm});
            skFitSpline(sketch, "E217", {"points": [v(17.65, 2.2) * mm, v(17.97, 2.1) * mm, v(18.44, 2.2) * mm, v(18.83, 2.51) * mm, v(18.88, 2.78) * mm], "startDerivative": vector(1.3, -0.56) * mm, "endDerivative": vector(0.05, 1.27) * mm});
            skFitSpline(sketch, "E218", {"points": [v(19.62, 3.34) * mm, v(18.88, 2.78) * mm], "startDerivative": vector(-0.74, -0.56) * mm, "endDerivative": vector(-0.74, -0.56) * mm});
            skFitSpline(sketch, "E219", {"points": [v(19.97, 3.2) * mm, v(20.2, 3.13) * mm], "startDerivative": vector(0.23, -0.06) * mm, "endDerivative": vector(0.23, -0.06) * mm});
            skFitSpline(sketch, "E220", {"points": [v(19.97, 3.2) * mm, v(19.81, 2.97) * mm, v(19.53, 2.74) * mm, v(19.29, 2.6) * mm], "startDerivative": vector(-0.44, -0.7) * mm, "endDerivative": vector(-0.73, -0.39) * mm});
            skFitSpline(sketch, "E221", {"points": [v(19.29, 2.6) * mm, v(19.39, 2.51) * mm, v(18.96, 2.12) * mm, v(19.55, 2.3) * mm], "startDerivative": vector(0.9, -0.3) * mm, "endDerivative": vector(2.26, 0.9) * mm});
            skFitSpline(sketch, "E222", {"points": [v(19.55, 2.3) * mm, v(19.55, 2.51) * mm, v(20.2, 3.13) * mm], "startDerivative": vector(-0.16, 0.6) * mm, "endDerivative": vector(1.31, 1) * mm});
            skFitSpline(sketch, "E223", {"points": [v(8.42, 26.63) * mm, v(8.18, 26.33) * mm, v(7.9, 25.68) * mm], "startDerivative": vector(-0.6, -0.61) * mm, "endDerivative": vector(-0.46, -1.26) * mm});
            skFitSpline(sketch, "E224", {"points": [v(7.97, 25.68) * mm, v(8.33, 25.77) * mm], "startDerivative": vector(0.36, 0.1) * mm, "endDerivative": vector(0.36, 0.1) * mm});
            skFitSpline(sketch, "E225", {"points": [v(7.97, 25.68) * mm, v(7.9, 25.68) * mm], "startDerivative": vector(-0.07, 0) * mm, "endDerivative": vector(-0.07, 0) * mm});
            skFitSpline(sketch, "E226", {"points": [v(8.33, 25.77) * mm, v(8.57, 26.42) * mm, v(8.83, 26.83) * mm, v(8.42, 26.63) * mm], "startDerivative": vector(0.43, 1.71) * mm, "endDerivative": vector(-1.92, -1.15) * mm});
            skFitSpline(sketch, "E227", {"points": [v(8.95, 25.9) * mm, v(9.41, 25.9) * mm, v(9.7, 26.4) * mm, v(9.73, 26.8) * mm, v(10.14, 27.32) * mm, v(9.69, 27.3) * mm, v(9.57, 27.06) * mm, v(9.34, 26.86) * mm, v(9.35, 26.63) * mm, v(9.24, 26.32) * mm, v(8.95, 25.9) * mm]});
            skLineSegment(sketch, "E228", {"start": v(10.14, 25.98) * mm, "end": v(10.57, 25.98) * mm});
            skFitSpline(sketch, "E229", {"points": [v(10.57, 25.98) * mm, v(10.7, 26.25) * mm, v(10.96, 26.74) * mm, v(10.9, 27.03) * mm], "startDerivative": vector(0.38, 0.81) * mm, "endDerivative": vector(-0.4, 0.9) * mm});
            skFitSpline(sketch, "E230", {"points": [v(10.9, 27.03) * mm, v(11.2, 27.6) * mm], "startDerivative": vector(0.31, 0.57) * mm, "endDerivative": vector(0.31, 0.57) * mm});
            skLineSegment(sketch, "E231", {"start": v(11.2, 27.6) * mm, "end": v(10.7, 27.48) * mm});
            skFitSpline(sketch, "E232", {"points": [v(10.7, 27.48) * mm, v(10.7, 27.28) * mm, v(10.39, 26.97) * mm], "startDerivative": vector(0.1, -0.5) * mm, "endDerivative": vector(-0.68, -0.53) * mm});
            skFitSpline(sketch, "E233", {"points": [v(10.39, 26.97) * mm, v(10.5, 26.84) * mm, v(10.39, 26.48) * mm, v(10.14, 25.98) * mm], "startDerivative": vector(0.63, -0.46) * mm, "endDerivative": vector(-0.58, -1.2) * mm});
            skLineSegment(sketch, "E234", {"start": v(11.47, 26) * mm, "end": v(11.94, 26) * mm});
            skFitSpline(sketch, "E235", {"points": [v(11.94, 26) * mm, v(12.04, 26.19) * mm, v(12.1, 26.72) * mm, v(11.94, 27.04) * mm], "startDerivative": vector(0.4, 0.6) * mm, "endDerivative": vector(-0.66, 0.83) * mm});
            skFitSpline(sketch, "E236", {"points": [v(11.94, 27.04) * mm, v(12.13, 27.24) * mm, v(12.33, 27.73) * mm], "startDerivative": vector(0.48, 0.4) * mm, "endDerivative": vector(0.31, 0.95) * mm});
            skLineSegment(sketch, "E237", {"start": v(12.33, 27.73) * mm, "end": v(11.89, 27.73) * mm});
            skFitSpline(sketch, "E238", {"points": [v(11.89, 27.73) * mm, v(11.89, 27.42) * mm, v(11.58, 27.13) * mm], "startDerivative": vector(0.13, -0.7) * mm, "endDerivative": vector(-0.73, -0.5) * mm});
            skFitSpline(sketch, "E239", {"points": [v(11.58, 27.13) * mm, v(11.66, 26.92) * mm, v(11.7, 26.52) * mm, v(11.47, 26) * mm], "startDerivative": vector(0.32, -0.75) * mm, "endDerivative": vector(-0.75, -1.3) * mm});
            skLineSegment(sketch, "E240", {"start": v(12.86, 26.03) * mm, "end": v(13.4, 26.03) * mm});
            skPoint(sketch, "E241.3.internal.snap0", {"position": v(13.13, 26.03) * mm});
            skFitSpline(sketch, "E241", {"points": [v(13.4, 26.03) * mm, v(13.4, 26.3) * mm, v(13.24, 26.98) * mm, v(13.13, 27.1) * mm], "startDerivative": vector(0.05, 0.73) * mm, "endDerivative": vector(-0.52, 0.28) * mm});
            skFitSpline(sketch, "E242", {"points": [v(13.13, 27.1) * mm, v(13.4, 27.34) * mm, v(13.68, 27.8) * mm], "startDerivative": vector(0.6, 0.5) * mm, "endDerivative": vector(0.52, 0.9) * mm});
            skLineSegment(sketch, "E243", {"start": v(13.68, 27.8) * mm, "end": v(13.21, 27.8) * mm});
            skFitSpline(sketch, "E244", {"points": [v(13.21, 27.8) * mm, v(13.1, 27.63) * mm, v(12.65, 27.16) * mm], "startDerivative": vector(-0.27, -0.4) * mm, "endDerivative": vector(-0.8, -0.83) * mm});
            skFitSpline(sketch, "E245", {"points": [v(12.65, 27.16) * mm, v(12.84, 26.95) * mm, v(12.87, 26.56) * mm, v(12.86, 26.03) * mm], "startDerivative": vector(0.81, -0.65) * mm, "endDerivative": vector(-0.01, -1.4) * mm});
            skLineSegment(sketch, "E246", {"start": v(14.7, 26) * mm, "end": v(14.3, 26) * mm});
            skFitSpline(sketch, "E247", {"points": [v(14.3, 26) * mm, v(14.3, 26.3) * mm, v(14.25, 26.59) * mm, v(14.14, 26.9) * mm, v(13.86, 27.13) * mm], "startDerivative": vector(0.06, 1.3) * mm, "endDerivative": vector(-1.2, 0.82) * mm});
            skFitSpline(sketch, "E248", {"points": [v(13.86, 27.13) * mm, v(14.02, 27.28) * mm, v(14.27, 27.47) * mm, v(14.53, 27.7) * mm], "startDerivative": vector(0.49, 0.52) * mm, "endDerivative": vector(0.67, 0.68) * mm});
            skLineSegment(sketch, "E249", {"start": v(14.53, 27.7) * mm, "end": v(15, 27.7) * mm});
            skFitSpline(sketch, "E250", {"points": [v(15, 27.7) * mm, v(14.86, 27.57) * mm, v(14.62, 27.37) * mm, v(14.3, 27.14) * mm], "startDerivative": vector(-0.45, -0.5) * mm, "endDerivative": vector(-0.87, -0.58) * mm});
            skFitSpline(sketch, "E251", {"points": [v(14.3, 27.14) * mm, v(14.5, 27) * mm, v(14.65, 26.6) * mm, v(14.7, 26) * mm], "startDerivative": vector(0.83, -0.44) * mm, "endDerivative": vector(0.03, -1.55) * mm});
            skLineSegment(sketch, "E252", {"start": v(16.4, 27.63) * mm, "end": v(16.86, 27.54) * mm});
            skFitSpline(sketch, "E253", {"points": [v(16.86, 27.54) * mm, v(16.68, 27.38) * mm, v(16.4, 27.13) * mm, v(16.13, 26.94) * mm], "startDerivative": vector(-0.57, -0.53) * mm, "endDerivative": vector(-0.76, -0.55) * mm});
            skFitSpline(sketch, "E254", {"points": [v(16.13, 26.94) * mm, v(16.26, 26.8) * mm, v(16.4, 26.52) * mm, v(16.48, 26.18) * mm, v(16.5, 25.85) * mm], "startDerivative": vector(0.66, -0.55) * mm, "endDerivative": vector(0.03, -1.22) * mm});
            skLineSegment(sketch, "E255", {"start": v(16.5, 25.85) * mm, "end": v(16.04, 25.94) * mm});
            skFitSpline(sketch, "E256", {"points": [v(16.04, 25.94) * mm, v(16.04, 26.27) * mm, v(15.94, 26.69) * mm, v(15.67, 26.98) * mm], "startDerivative": vector(0.04, 1.02) * mm, "endDerivative": vector(-0.9, 0.76) * mm});
            skFitSpline(sketch, "E257", {"points": [v(15.67, 26.98) * mm, v(15.93, 27.19) * mm, v(16.23, 27.41) * mm, v(16.4, 27.63) * mm], "startDerivative": vector(0.73, 0.63) * mm, "endDerivative": vector(0.5, 0.72) * mm});
            skLineSegment(sketch, "E258", {"start": v(17.6, 27.37) * mm, "end": v(18.07, 27.28) * mm});
            skFitSpline(sketch, "E259", {"points": [v(18.07, 27.28) * mm, v(17.84, 27.08) * mm, v(17.5, 26.82) * mm, v(17.37, 26.74) * mm], "startDerivative": vector(-0.58, -0.53) * mm, "endDerivative": vector(-0.45, -0.24) * mm});
            skFitSpline(sketch, "E260", {"points": [v(17.37, 26.74) * mm, v(17.58, 26.58) * mm, v(17.71, 26.28) * mm, v(17.8, 25.87) * mm, v(17.82, 25.6) * mm], "startDerivative": vector(1.03, -0.6) * mm, "endDerivative": vector(-0.01, -1.08) * mm});
            skLineSegment(sketch, "E261", {"start": v(17.82, 25.6) * mm, "end": v(17.45, 25.63) * mm});
            skFitSpline(sketch, "E262", {"points": [v(17.45, 25.63) * mm, v(17.45, 25.85) * mm, v(17.33, 26.23) * mm, v(17.05, 26.76) * mm, v(16.98, 26.86) * mm], "startDerivative": vector(0.07, 1) * mm, "endDerivative": vector(-0.38, 0.5) * mm});
            skFitSpline(sketch, "E263", {"points": [v(17.6, 27.37) * mm, v(17.5, 27.25) * mm, v(17.23, 27.04) * mm, v(16.98, 26.86) * mm], "startDerivative": vector(-0.35, -0.42) * mm, "endDerivative": vector(-0.69, -0.46) * mm});
            skLineSegment(sketch, "E264", {"start": v(18.9, 27.02) * mm, "end": v(19.4, 26.93) * mm});
            skFitSpline(sketch, "E265", {"points": [v(19.4, 26.93) * mm, v(19.14, 26.71) * mm, v(18.87, 26.52) * mm], "startDerivative": vector(-0.51, -0.44) * mm, "endDerivative": vector(-0.54, -0.38) * mm});
            skFitSpline(sketch, "E266", {"points": [v(18.87, 26.52) * mm, v(19, 26.35) * mm, v(19.2, 25.83) * mm, v(19.24, 25.22) * mm], "startDerivative": vector(0.48, -0.63) * mm, "endDerivative": vector(-0.06, -1.53) * mm});
            skLineSegment(sketch, "E267", {"start": v(19.24, 25.22) * mm, "end": v(18.79, 25.34) * mm});
            skFitSpline(sketch, "E268", {"points": [v(18.79, 25.34) * mm, v(18.79, 25.74) * mm, v(18.6, 26.31) * mm, v(18.43, 26.57) * mm], "startDerivative": vector(0.12, 1.16) * mm, "endDerivative": vector(-0.56, 0.78) * mm});
            skFitSpline(sketch, "E269", {"points": [v(18.43, 26.57) * mm, v(18.63, 26.7) * mm, v(18.9, 27.02) * mm], "startDerivative": vector(0.47, 0.24) * mm, "endDerivative": vector(0.49, 0.64) * mm});
            skLineSegment(sketch, "E270", {"start": v(20.01, 25) * mm, "end": v(20.45, 24.81) * mm});
            skFitSpline(sketch, "E271", {"points": [v(20.45, 24.81) * mm, v(20.42, 25.37) * mm, v(20.23, 25.9) * mm, v(20.12, 26) * mm], "startDerivative": vector(0.03, 1.35) * mm, "endDerivative": vector(-0.5, 0.35) * mm});
            skLineSegment(sketch, "E272", {"start": v(20.21, 26.57) * mm, "end": v(20.63, 26.42) * mm});
            skFitSpline(sketch, "E273", {"points": [v(20.12, 26) * mm, v(20.3, 26.12) * mm, v(20.63, 26.42) * mm], "startDerivative": vector(0.39, 0.27) * mm, "endDerivative": vector(0.61, 0.55) * mm});
            skFitSpline(sketch, "E274", {"points": [v(20.21, 26.57) * mm, v(19.97, 26.34) * mm, v(19.72, 26.18) * mm], "startDerivative": vector(-0.47, -0.46) * mm, "endDerivative": vector(-0.53, -0.3) * mm});
            skFitSpline(sketch, "E275", {"points": [v(19.72, 26.18) * mm, v(19.88, 25.85) * mm, v(20.03, 25.28) * mm, v(20.01, 25) * mm], "startDerivative": vector(0.5, -0.93) * mm, "endDerivative": vector(-0.15, -0.89) * mm});
            skLineSegment(sketch, "E276", {"start": v(21.55, 26.07) * mm, "end": v(21.95, 25.9) * mm});
            skFitSpline(sketch, "E277", {"points": [v(21.95, 25.9) * mm, v(21.8, 25.76) * mm, v(21.46, 25.54) * mm], "startDerivative": vector(-0.29, -0.35) * mm, "endDerivative": vector(-0.66, -0.39) * mm});
            skFitSpline(sketch, "E278", {"points": [v(21.46, 25.54) * mm, v(21.73, 25.14) * mm, v(21.83, 24.27) * mm], "startDerivative": vector(0.72, -0.8) * mm, "endDerivative": vector(0.05, -1.68) * mm});
            skLineSegment(sketch, "E279", {"start": v(21.83, 24.27) * mm, "end": v(21.4, 24.45) * mm});
            skFitSpline(sketch, "E280", {"points": [v(21.4, 24.45) * mm, v(21.36, 25.1) * mm, v(21.03, 25.7) * mm], "startDerivative": vector(0.07, 1.33) * mm, "endDerivative": vector(-0.79, 1.16) * mm});
            skFitSpline(sketch, "E281", {"points": [v(21.55, 26.07) * mm, v(21.4, 25.94) * mm, v(21.03, 25.7) * mm], "startDerivative": vector(-0.33, -0.3) * mm, "endDerivative": vector(-0.67, -0.43) * mm});
            skLineSegment(sketch, "E282", {"start": v(22.63, 25.55) * mm, "end": v(23.03, 25.37) * mm});
            skFitSpline(sketch, "E283", {"points": [v(23.03, 25.37) * mm, v(22.78, 25.14) * mm, v(22.6, 25.04) * mm], "startDerivative": vector(-0.44, -0.46) * mm, "endDerivative": vector(-0.42, -0.18) * mm});
            skFitSpline(sketch, "E284", {"points": [v(22.6, 25.04) * mm, v(22.89, 24.56) * mm, v(22.97, 23.77) * mm], "startDerivative": vector(0.74, -0.97) * mm, "endDerivative": vector(0.02, -1.55) * mm});
            skLineSegment(sketch, "E285", {"start": v(22.97, 23.77) * mm, "end": v(22.5, 24.02) * mm});
            skFitSpline(sketch, "E286", {"points": [v(22.5, 24.02) * mm, v(22.45, 24.64) * mm, v(22.14, 25.2) * mm], "startDerivative": vector(0, 1.28) * mm, "endDerivative": vector(-0.73, 1.06) * mm});
            skFitSpline(sketch, "E287", {"points": [v(22.63, 25.55) * mm, v(22.45, 25.38) * mm, v(22.14, 25.2) * mm], "startDerivative": vector(-0.35, -0.4) * mm, "endDerivative": vector(-0.6, -0.33) * mm});
            skLineSegment(sketch, "E288", {"start": v(23.68, 24.91) * mm, "end": v(24.04, 24.71) * mm});
            skFitSpline(sketch, "E289", {"points": [v(24.04, 24.71) * mm, v(23.77, 24.44) * mm], "startDerivative": vector(-0.28, -0.27) * mm, "endDerivative": vector(-0.28, -0.27) * mm});
            skFitSpline(sketch, "E290", {"points": [v(23.77, 24.44) * mm, v(23.98, 24.08) * mm, v(24.1, 23) * mm], "startDerivative": vector(0.62, -0.78) * mm, "endDerivative": vector(0.1, -2) * mm});
            skLineSegment(sketch, "E291", {"start": v(24.1, 23) * mm, "end": v(23.68, 23.24) * mm});
            skFitSpline(sketch, "E292", {"points": [v(23.68, 23.24) * mm, v(23.6, 24.05) * mm, v(23.33, 24.6) * mm], "startDerivative": vector(-0.03, 1.6) * mm, "endDerivative": vector(-0.7, 1.11) * mm});
            skFitSpline(sketch, "E293", {"points": [v(23.68, 24.91) * mm, v(23.54, 24.76) * mm, v(23.33, 24.6) * mm], "startDerivative": vector(-0.28, -0.34) * mm, "endDerivative": vector(-0.42, -0.27) * mm});
            skLineSegment(sketch, "E294", {"start": v(24.86, 24.2) * mm, "end": v(25.11, 23.9) * mm});
            skFitSpline(sketch, "E295", {"points": [v(25.11, 23.9) * mm, v(24.9, 23.7) * mm], "startDerivative": vector(-0.22, -0.2) * mm, "endDerivative": vector(-0.22, -0.2) * mm});
            skFitSpline(sketch, "E296", {"points": [v(24.9, 23.7) * mm, v(25.01, 23.3) * mm, v(25.11, 22.8) * mm, v(25.11, 22.19) * mm], "startDerivative": vector(0.39, -1.3) * mm, "endDerivative": vector(-0.08, -1.74) * mm});
            skLineSegment(sketch, "E297", {"start": v(25.11, 22.19) * mm, "end": v(24.68, 22.44) * mm});
            skFitSpline(sketch, "E298", {"points": [v(24.68, 22.44) * mm, v(24.68, 23.12) * mm, v(24.48, 23.84) * mm], "startDerivative": vector(0.1, 1.38) * mm, "endDerivative": vector(-0.48, 1.42) * mm});
            skFitSpline(sketch, "E299", {"points": [v(24.86, 24.2) * mm, v(24.48, 23.84) * mm], "startDerivative": vector(-0.38, -0.35) * mm, "endDerivative": vector(-0.38, -0.35) * mm});
            skFitSpline(sketch, "E300", {"points": [v(25.85, 23.32) * mm, v(25.57, 23.04) * mm], "startDerivative": vector(-0.28, -0.28) * mm, "endDerivative": vector(-0.28, -0.28) * mm});
            skFitSpline(sketch, "E301", {"points": [v(25.57, 23.04) * mm, v(25.66, 22.48) * mm, v(25.67, 21.78) * mm], "startDerivative": vector(0.22, -1.15) * mm, "endDerivative": vector(-0.02, -1.36) * mm});
            skLineSegment(sketch, "E302", {"start": v(25.67, 21.78) * mm, "end": v(26, 21.45) * mm});
            skFitSpline(sketch, "E303", {"points": [v(26, 21.45) * mm, v(26.03, 22.22) * mm, v(25.93, 22.72) * mm], "startDerivative": vector(0.13, 1.47) * mm, "endDerivative": vector(-0.28, 1.05) * mm});
            skLineSegment(sketch, "E304", {"start": v(25.93, 22.72) * mm, "end": v(26.17, 23) * mm});
            skLineSegment(sketch, "E305", {"start": v(25.85, 23.32) * mm, "end": v(26.17, 23) * mm});
            skLineSegment(sketch, "E306", {"start": v(26.63, 22.29) * mm, "end": v(26.92, 21.86) * mm});
            skFitSpline(sketch, "E307", {"points": [v(26.92, 21.86) * mm, v(26.84, 21.4) * mm, v(26.66, 20.74) * mm], "startDerivative": vector(-0.15, -0.98) * mm, "endDerivative": vector(-0.36, -1.26) * mm});
            skLineSegment(sketch, "E308", {"start": v(26.66, 20.74) * mm, "end": v(26.34, 21.07) * mm});
            skFitSpline(sketch, "E309", {"points": [v(26.63, 22.29) * mm, v(26.53, 21.67) * mm, v(26.34, 21.07) * mm], "startDerivative": vector(-0.16, -1.24) * mm, "endDerivative": vector(-0.43, -1.2) * mm});
            skFitSpline(sketch, "E310", {"points": [v(27.24, 21.44) * mm, v(27.23, 20.78) * mm, v(27, 20.24) * mm], "startDerivative": vector(0.11, -1.32) * mm, "endDerivative": vector(-0.6, -1.08) * mm});
            skLineSegment(sketch, "E311", {"start": v(27, 20.24) * mm, "end": v(27.15, 19.82) * mm});
            skFitSpline(sketch, "E312", {"points": [v(27.15, 19.82) * mm, v(27.35, 20.18) * mm, v(27.53, 20.95) * mm], "startDerivative": vector(0.5, 0.76) * mm, "endDerivative": vector(0.27, 1.46) * mm});
            skFitSpline(sketch, "E313", {"points": [v(27.24, 21.44) * mm, v(27.53, 20.95) * mm], "startDerivative": vector(0.3, -0.49) * mm, "endDerivative": vector(0.3, -0.49) * mm});
            skFitSpline(sketch, "E314", {"points": [v(14.25, 4.43) * mm, v(14.79, 4.46) * mm, v(15.92, 4.55) * mm], "startDerivative": vector(1.19, 0.04) * mm, "endDerivative": vector(2.09, 0.18) * mm});
            skLineSegment(sketch, "E315", {"start": v(15.92, 4.55) * mm, "end": v(16.1, 4.37) * mm});
            skFitSpline(sketch, "E316", {"points": [v(14.51, 4.14) * mm, v(15.2, 4.17) * mm, v(16.1, 4.37) * mm], "startDerivative": vector(1.43, 0) * mm, "endDerivative": vector(1.73, 0.44) * mm});
            skFitSpline(sketch, "E317", {"points": [v(18.36, 4.17) * mm, v(17.93, 3.74) * mm, v(17.47, 3.44) * mm], "startDerivative": vector(-0.8, -0.9) * mm, "endDerivative": vector(-0.98, -0.55) * mm});
            skFitSpline(sketch, "E318", {"points": [v(17.47, 3.44) * mm, v(17.56, 3.3) * mm, v(17.36, 3.1) * mm, v(16.41, 2.74) * mm], "startDerivative": vector(0.66, -0.67) * mm, "endDerivative": vector(-2.1, -0.7) * mm});
            skFitSpline(sketch, "E319", {"points": [v(16.04, 2.93) * mm, v(16.64, 3.08) * mm, v(17.25, 3.37) * mm, v(17.22, 3.52) * mm], "startDerivative": vector(1.38, 0.33) * mm, "endDerivative": vector(-0.46, 0.8) * mm});
            skFitSpline(sketch, "E320", {"points": [v(16.94, 3.69) * mm, v(16.79, 3.85) * mm], "startDerivative": vector(-0.15, 0.16) * mm, "endDerivative": vector(-0.15, 0.16) * mm});
            skFitSpline(sketch, "E321", {"points": [v(16.79, 3.85) * mm, v(17.26, 4.33) * mm, v(17.62, 4.81) * mm], "startDerivative": vector(0.97, 0.93) * mm, "endDerivative": vector(0.7, 1) * mm});
            skSolve(sketch);
        }
        {
            var Q0;
            Q0=qSketchRegion(id+"F8",true);
            extrude(context, id + "F9", {"entities" : qUnion([Q0]), "operationType" : NewBodyOperationType.ADD, "depth" : 3 * mm, "offsetDistance" : 25.4 * mm});
        }
        {
            var Q0;
            Q0=makeQuery(id+"F4.opExtrude","CAP_FACE",FACE,{"disambiguationData":[OSD([sQuery(id+"F1.wireOp",EDGE,"E4"),sQuery(id+"F1.wireOp",EDGE,"E5"),sQuery(id+"F1.wireOp",EDGE,"E6"),sQuery(id+"F1.wireOp",EDGE,"E7"),sQuery(id+"F1.wireOp",EDGE,"E8"),sQuery(id+"F1.wireOp",EDGE,"E9"),sQuery(id+"F1.wireOp",EDGE,"E10"),sQuery(id+"F1.wireOp",EDGE,"E11"),sQuery(id+"F1.wireOp",EDGE,"E12"),sQuery(id+"F1.wireOp",EDGE,"E13"),sQuery(id+"F1.wireOp",EDGE,"E14"),sQuery(id+"F1.wireOp",EDGE,"E15"),sQuery(id+"F1.wireOp",EDGE,"E16"),sQuery(id+"F1.wireOp",EDGE,"E17"),sQuery(id+"F1.wireOp",EDGE,"E18"),sQuery(id+"F1.wireOp",EDGE,"E19"),sQuery(id+"F1.wireOp",EDGE,"E20"),sQuery(id+"F1.wireOp",EDGE,"E21"),sQuery(id+"F1.wireOp",EDGE,"E22"),sQuery(id+"F1.wireOp",EDGE,"E23"),sQuery(id+"F1.wireOp",EDGE,"E24"),sQuery(id+"F1.wireOp",EDGE,"E25"),sQuery(id+"F1.wireOp",EDGE,"E26"),sQuery(id+"F1.wireOp",EDGE,"E27"),sQuery(id+"F1.wireOp",EDGE,"E28"),sQuery(id+"F1.wireOp",EDGE,"E29"),sQuery(id+"F1.wireOp",EDGE,"E30"),sQuery(id+"F1.wireOp",EDGE,"E31"),sQuery(id+"F1.wireOp",EDGE,"E32"),sQuery(id+"F1.wireOp",EDGE,"E33"),sQuery(id+"F1.wireOp",EDGE,"E34"),sQuery(id+"F1.wireOp",EDGE,"E35"),sQuery(id+"F1.wireOp",EDGE,"E36"),sQuery(id+"F1.wireOp",EDGE,"E37"),sQuery(id+"F1.wireOp",EDGE,"E38"),sQuery(id+"F1.wireOp",EDGE,"E39"),sQuery(id+"F1.wireOp",EDGE,"E40"),sQuery(id+"F1.wireOp",EDGE,"E41"),sQuery(id+"F1.wireOp",EDGE,"E42"),sQuery(id+"F1.wireOp",EDGE,"E43"),sQuery(id+"F1.wireOp",EDGE,"E44"),sQuery(id+"F1.wireOp",EDGE,"E45"),sQuery(id+"F1.wireOp",EDGE,"E46"),sQuery(id+"F1.wireOp",EDGE,"E47"),sQuery(id+"F1.wireOp",EDGE,"E48"),sQuery(id+"F1.wireOp",EDGE,"E49"),sQuery(id+"F1.wireOp",EDGE,"E50"),sQuery(id+"F1.wireOp",EDGE,"E51"),sQuery(id+"F1.wireOp",EDGE,"E52"),sQuery(id+"F1.wireOp",EDGE,"E53"),sQuery(id+"F1.wireOp",EDGE,"E54"),sQuery(id+"F1.wireOp",EDGE,"E55"),sQuery(id+"F1.wireOp",EDGE,"E56"),sQuery(id+"F1.wireOp",EDGE,"E57"),sQuery(id+"F1.wireOp",EDGE,"E58"),sQuery(id+"F1.wireOp",EDGE,"E59"),sQuery(id+"F1.wireOp",EDGE,"E60"),sQuery(id+"F1.wireOp",EDGE,"E61"),sQuery(id+"F1.wireOp",EDGE,"E62"),sQuery(id+"F1.wireOp",EDGE,"E63"),sQuery(id+"F1.wireOp",EDGE,"E64"),sQuery(id+"F1.wireOp",EDGE,"E65"),sQuery(id+"F1.wireOp",EDGE,"E66"),sQuery(id+"F1.wireOp",EDGE,"E67"),sQuery(id+"F1.wireOp",EDGE,"E68"),sQuery(id+"F1.wireOp",EDGE,"E69"),sQuery(id+"F1.wireOp",EDGE,"E70"),sQuery(id+"F1.wireOp",EDGE,"E71"),sQuery(id+"F1.wireOp",EDGE,"E72"),sQuery(id+"F1.wireOp",EDGE,"E73"),sQuery(id+"F1.wireOp",EDGE,"E74"),sQuery(id+"F1.wireOp",EDGE,"E75"),sQuery(id+"F1.wireOp",EDGE,"E76"),sQuery(id+"F1.wireOp",EDGE,"E77"),sQuery(id+"F1.wireOp",EDGE,"E78"),sQuery(id+"F1.wireOp",EDGE,"E79"),sQuery(id+"F1.wireOp",EDGE,"E80"),sQuery(id+"F1.wireOp",EDGE,"E81"),sQuery(id+"F1.wireOp",EDGE,"E82"),sQuery(id+"F1.wireOp",EDGE,"E83"),sQuery(id+"F1.wireOp",EDGE,"E84"),sQuery(id+"F1.wireOp",EDGE,"E85"),sQuery(id+"F1.wireOp",EDGE,"E86")])],"isStart":false});
            var sketch = newSketch(context, id + "F10", { "sketchPlane" : qUnion([Q0])});
            skLineSegment(sketch, "E322", {"start": v(3.7, 9.8) * mm, "end": v(4.53, 9.8) * mm});
            skFitSpline(sketch, "E323", {"points": [v(4.53, 9.8) * mm, v(6.33, 8.67) * mm, v(11.57, 6.98) * mm, v(13.85, 6.7) * mm, v(16.87, 6.66) * mm, v(22.8, 8.09) * mm, v(26.18, 10.02) * mm], "startDerivative": vector(11.2, -8.61) * mm, "endDerivative": vector(17.33, 11.9) * mm});
            skLineSegment(sketch, "E324", {"start": v(26.18, 10.02) * mm, "end": v(27.02, 10.02) * mm});
            skLineSegment(sketch, "E325", {"start": v(27.02, 10.02) * mm, "end": v(27.47, 9.51) * mm});
            skLineSegment(sketch, "E326", {"start": v(27.47, 9.51) * mm, "end": v(24.71, 5.76) * mm});
            skLineSegment(sketch, "E327", {"start": v(24.71, 5.76) * mm, "end": v(5.75, 5.76) * mm});
            skLineSegment(sketch, "E328", {"start": v(5.75, 5.76) * mm, "end": v(3.34, 9.32) * mm});
            skLineSegment(sketch, "E329", {"start": v(3.34, 9.32) * mm, "end": v(3.7, 9.8) * mm});
            skLineSegment(sketch, "E330", {"start": v(4.29, 9.52) * mm, "end": v(4.62, 9.52) * mm});
            skFitSpline(sketch, "E331", {"points": [v(4.62, 9.52) * mm, v(4.93, 9.17) * mm, v(5.49, 8.83) * mm], "startDerivative": vector(0.6, -0.8) * mm, "endDerivative": vector(1.12, -0.6) * mm});
            skLineSegment(sketch, "E332", {"start": v(5.49, 8.83) * mm, "end": v(5.49, 6.34) * mm});
            skLineSegment(sketch, "E333", {"start": v(5.49, 6.34) * mm, "end": v(5.49, 6.14) * mm});
            skLineSegment(sketch, "E334", {"start": v(5.49, 6.14) * mm, "end": v(4.25, 7.96) * mm});
            skLineSegment(sketch, "E335", {"start": v(4.25, 7.96) * mm, "end": v(4.29, 9.52) * mm});
            skFitSpline(sketch, "E336", {"points": [v(5.67, 8.76) * mm, v(6.5, 8.34) * mm], "startDerivative": vector(0.83, -0.42) * mm, "endDerivative": vector(0.83, -0.42) * mm});
            skLineSegment(sketch, "E337", {"start": v(6.5, 8.34) * mm, "end": v(6.5, 6.09) * mm});
            skLineSegment(sketch, "E338", {"start": v(6.5, 6.09) * mm, "end": v(5.66, 6.09) * mm});
            skLineSegment(sketch, "E339", {"start": v(5.66, 6.09) * mm, "end": v(5.67, 8.76) * mm});
            skLineSegment(sketch, "E340", {"start": v(6.75, 8.2) * mm, "end": v(7.6, 7.85) * mm});
            skLineSegment(sketch, "E341", {"start": v(7.6, 7.85) * mm, "end": v(7.6, 6.12) * mm});
            skLineSegment(sketch, "E342", {"start": v(7.6, 6.12) * mm, "end": v(6.75, 6.12) * mm});
            skLineSegment(sketch, "E343", {"start": v(6.75, 6.12) * mm, "end": v(6.75, 8.2) * mm});
            skLineSegment(sketch, "E344", {"start": v(7.81, 7.76) * mm, "end": v(8.64, 7.48) * mm});
            skLineSegment(sketch, "E345", {"start": v(8.64, 7.48) * mm, "end": v(8.64, 6.1) * mm});
            skLineSegment(sketch, "E346", {"start": v(8.64, 6.1) * mm, "end": v(7.8, 6.1) * mm});
            skLineSegment(sketch, "E347", {"start": v(7.8, 6.1) * mm, "end": v(7.81, 7.76) * mm});
            skLineSegment(sketch, "E348", {"start": v(8.88, 7.39) * mm, "end": v(9.7, 7.18) * mm});
            skLineSegment(sketch, "E349", {"start": v(9.7, 7.18) * mm, "end": v(9.74, 6.08) * mm});
            skLineSegment(sketch, "E350", {"start": v(9.74, 6.08) * mm, "end": v(8.9, 6.08) * mm});
            skLineSegment(sketch, "E351", {"start": v(8.9, 6.08) * mm, "end": v(8.88, 7.39) * mm});
            skLineSegment(sketch, "E352", {"start": v(10, 7.13) * mm, "end": v(10.8, 6.93) * mm});
            skLineSegment(sketch, "E353", {"start": v(10.8, 6.93) * mm, "end": v(10.84, 6.07) * mm});
            skLineSegment(sketch, "E354", {"start": v(10.84, 6.07) * mm, "end": v(9.93, 6.07) * mm});
            skLineSegment(sketch, "E355", {"start": v(9.93, 6.07) * mm, "end": v(10, 7.13) * mm});
            skLineSegment(sketch, "E356", {"start": v(11.1, 6.88) * mm, "end": v(11.86, 6.74) * mm});
            skLineSegment(sketch, "E357", {"start": v(11.86, 6.74) * mm, "end": v(11.88, 6.04) * mm});
            skLineSegment(sketch, "E358", {"start": v(11.88, 6.04) * mm, "end": v(11.08, 6.04) * mm});
            skLineSegment(sketch, "E359", {"start": v(11.08, 6.04) * mm, "end": v(11.1, 6.88) * mm});
            skLineSegment(sketch, "E360", {"start": v(12.13, 6.7) * mm, "end": v(12.13, 6.06) * mm});
            skLineSegment(sketch, "E361", {"start": v(12.13, 6.06) * mm, "end": v(18.67, 6.06) * mm});
            skLineSegment(sketch, "E362", {"start": v(18.67, 6.06) * mm, "end": v(18.64, 6.71) * mm});
            skFitSpline(sketch, "E363", {"points": [v(18.64, 6.71) * mm, v(17.58, 6.57) * mm, v(15.49, 6.4) * mm, v(13.58, 6.5) * mm, v(12.13, 6.7) * mm], "startDerivative": vector(-4.74, -0.64) * mm, "endDerivative": vector(-5.9, 0.88) * mm});
            skLineSegment(sketch, "E364", {"start": v(18.86, 6.76) * mm, "end": v(19.73, 6.94) * mm});
            skLineSegment(sketch, "E365", {"start": v(19.73, 6.94) * mm, "end": v(19.73, 6.02) * mm});
            skLineSegment(sketch, "E366", {"start": v(19.73, 6.02) * mm, "end": v(18.87, 6.02) * mm});
            skLineSegment(sketch, "E367", {"start": v(18.87, 6.02) * mm, "end": v(18.86, 6.76) * mm});
            skLineSegment(sketch, "E368", {"start": v(19.93, 6.99) * mm, "end": v(20.77, 7.23) * mm});
            skLineSegment(sketch, "E369", {"start": v(20.77, 7.23) * mm, "end": v(20.77, 6.02) * mm});
            skLineSegment(sketch, "E370", {"start": v(20.77, 6.02) * mm, "end": v(19.95, 6.02) * mm});
            skLineSegment(sketch, "E371", {"start": v(19.95, 6.02) * mm, "end": v(19.93, 6.99) * mm});
            skLineSegment(sketch, "E372", {"start": v(21.03, 7.25) * mm, "end": v(21.88, 7.56) * mm});
            skLineSegment(sketch, "E373", {"start": v(21.88, 7.56) * mm, "end": v(21.88, 6.06) * mm});
            skLineSegment(sketch, "E374", {"start": v(21.88, 6.06) * mm, "end": v(21.07, 6.06) * mm});
            skLineSegment(sketch, "E375", {"start": v(21.07, 6.06) * mm, "end": v(21.03, 7.25) * mm});
            skLineSegment(sketch, "E376", {"start": v(22.1, 7.63) * mm, "end": v(22.93, 7.94) * mm});
            skLineSegment(sketch, "E377", {"start": v(22.93, 7.94) * mm, "end": v(22.93, 6.04) * mm});
            skLineSegment(sketch, "E378", {"start": v(22.93, 6.04) * mm, "end": v(22.1, 6.04) * mm});
            skLineSegment(sketch, "E379", {"start": v(22.1, 6.04) * mm, "end": v(22.1, 7.63) * mm});
            skLineSegment(sketch, "E380", {"start": v(23.1, 8.03) * mm, "end": v(24, 8.43) * mm});
            skLineSegment(sketch, "E381", {"start": v(24, 8.43) * mm, "end": v(24, 6.02) * mm});
            skLineSegment(sketch, "E382", {"start": v(24, 6.02) * mm, "end": v(23.16, 6.02) * mm});
            skLineSegment(sketch, "E383", {"start": v(23.16, 6.02) * mm, "end": v(23.1, 8.03) * mm});
            skLineSegment(sketch, "E384", {"start": v(24.26, 8.52) * mm, "end": v(25.09, 9) * mm});
            skLineSegment(sketch, "E385", {"start": v(25.09, 9) * mm, "end": v(25.09, 6.42) * mm});
            skLineSegment(sketch, "E386", {"start": v(25.09, 6.42) * mm, "end": v(24.6, 6) * mm});
            skLineSegment(sketch, "E387", {"start": v(24.6, 6) * mm, "end": v(24.25, 6) * mm});
            skLineSegment(sketch, "E388", {"start": v(24.25, 6) * mm, "end": v(24.26, 8.52) * mm});
            skLineSegment(sketch, "E389", {"start": v(25.32, 9.13) * mm, "end": v(26.25, 9.84) * mm});
            skLineSegment(sketch, "E390", {"start": v(26.25, 9.84) * mm, "end": v(26.45, 9.83) * mm});
            skLineSegment(sketch, "E391", {"start": v(26.45, 9.83) * mm, "end": v(26.45, 8.2) * mm});
            skLineSegment(sketch, "E392", {"start": v(26.45, 8.2) * mm, "end": v(25.34, 6.76) * mm});
            skLineSegment(sketch, "E393", {"start": v(25.34, 6.76) * mm, "end": v(25.32, 9.13) * mm});
            skSolve(sketch);
        }
        {
            var Q0;
            Q0=qSketchRegion(id+"F10",true);
            extrude(context, id + "F11", {"entities" : qUnion([Q0]), "operationType" : NewBodyOperationType.ADD, "depth" : 1 * mm, "offsetDistance" : 25.4 * mm});
        }
        {
            var Q0;
            Q0=makeQuery(id+"F3.opExtrude","SWEPT_EDGE",EDGE,{"disambiguationData":[OSD([sQuery(id+"F0.wireOp",EDGE,"E3.top"),sQuery(id+"F0.wireOp",EDGE,"E3.right")])]});
            var Q1;
            Q1=makeQuery(id+"F3.opExtrude","SWEPT_EDGE",EDGE,{"disambiguationData":[OSD([sQuery(id+"F0.wireOp",EDGE,"E3.top"),sQuery(id+"F0.wireOp",EDGE,"E3.left")])]});
            chamfer(context, id + "F12", {"entities" : qUnion([Q0, Q1]), "width" : 3 * mm, "tangentPropagation" : true});
        }
        {
            var Q0;
            Q0=makeQuery(id+"F3.opExtrude","CAP_EDGE",EDGE,{"disambiguationData":[OSD([sQuery(id+"F0.wireOp",EDGE,"E2")])],"isStart":false});
            fillet(context, id + "F13", {"entities" : qUnion([Q0]), "radius" : 1 * mm, "tangentPropagation" : true, "allowEdgeOverflow" : false});
        }
    });
